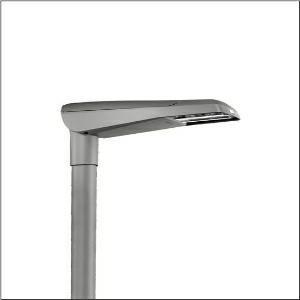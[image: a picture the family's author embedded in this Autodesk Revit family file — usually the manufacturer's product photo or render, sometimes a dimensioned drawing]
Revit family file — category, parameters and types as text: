
# Revit family: streetlight_sl_11_iq_micro___st0_5a_5xc1b51e08ce_0c76
name_source: partatom
category: Lighting Fixtures
units: mm (PartAtom-declared; Revit-internal decimal feet)

## family parameters
Cut with Voids When Loaded = No
Host = Face
Light Source = No
Part Type = Normal
Room Calculation Point = No
Round Connector Dimension = Use Diameter
Shared = No

## types (1)
- --- (1 x LED, 1860 lm, 12.6 W, 3000K)
    Apparent Load = 13 VA
    CIE Flux Codes = 42 72 97 100 100
    Color Rendering = 70
    Color Temperature = 3000K
    Default Elevation = 1800 mm
    Description = Streetlight SL 11 iQ micro, mast luminaire, primary light control with 3 zone facetted reflector, of plastic, silver coated, highly specular, primary optical cover: cover, of PMMA, transparent, light distribution: ST0.5a, light emission: direct distribution, primary light characteristic: asymmetric, installation type: post-top, side-entry, lamps: LED, High Power LED, rated values: 1.860lm | 12,6W | 147,6lm/W (begin service life); end service life: 1.860lm | 12,9W; at 50% lumin. flux: 930lm | 6,8W | 136,8lm/W, colour temperature: 3000K, colour rendering: CRI > 70, light colour: 730, light setting 1 begin service life: 100% | 1.860lm | 12,6W | 147,6lm/W | 3.000K, light setting 1 end service life: 12,9W, further light settings possible, control: optimised constant luminous flux control (CLO 2.0), Desk-Remote (wireless, voltage-free reading and setting of iQ features in the workshop via application-optimized NFC function/RFID function), Light-Fading, Smart-Wire, Night-Set, Lumen-Switch, Temp-Guard, Auto-Match, with cable H07RN-F 5x 1.5mm², mains connection: 230..240V, AC, 50/60Hz, connection cable pre-assembled, cable length: 5,5m, luminaire housing, of diecast aluminium, powder-coated, Siteco® metallic grey (DB 702S), please order mast flange separately, inclination adjustable without tools: 0°, 5°, 10°, 15° (post-top) | 0°, -5°, -10°, -15° (side-entry), sealing non-destructively replaceable, multi-level sealing system, length: 600mm, width: 174mm, height: 116mm, mast flange for spigot size: 42mm (side-entry): 5XC10008XM4, 60/48mm (side-entry/post-top): 5XC10108XM2, 76/60mm (side-entry/post-top): 5XC10108XM1, equipment: standard, protection rating (complete): IP66, insulation class (complete): insulation class II (safety insulation), certification: CE, ENEC, ENEC+, VDE, impact resistance: IK10, permissible operating ambient temperature for outdoor applications: -25..+50°C, standard-compliant lighting for roads and squares, Environmental Product Declaration (EPD) tested and certified by an independent institute, packaging unit: 1 piece

Light Distribution: ST0.5a
    Height = 116 mm
    Lamp = 1 x LED
    Lamp Light Flux = 1860 lm
    Lamp Power = 12.6 W
    Lamp count = 1
    Length = 600 mm
    Luminous efficacy = 148 lm/W
    Manufacturer = Siteco
    ModVariant = No
    Model = 5XC1B51E08CE
    Number of Poles = 1
    OnlyDefault = Yes
    Power Factor = 1
    Product Name = Streetlight SL 11 iQ micro | ST0.5a
    Product group = mast luminaire | pylon top
    ProductGroupID = 6100
    Protection Class = Protection class II
    Protection Degree = IP 66
    RLX_Detail_Level = 1
    RLX_Emergency_Light_Flux = 0 lm
    RLX_Emergency_Type = 0
    RLX_Emergency_Type_DB = No
    RlxData = <blob elided: 26793 chars, md5=819d0120>
    Socket = socket
    Standby Power = 0 W
    System Light Flux = 1860 lm
    System Power = 13 W
    Type Comments = factory setting: luminous flux: 100 % | dim-lin: 254 | 229 mA
    Type Image = l_1006566.jpg
    URL = http://relux.com
    VarID = @adj_020691
    Voltage = 0 V
    Weight = 0.00 kg
    Width = 174 mm

## geometry (parser evidence)
native form markers: Blend x4, Sweep x11
no freeform markers — native parametric forms only
